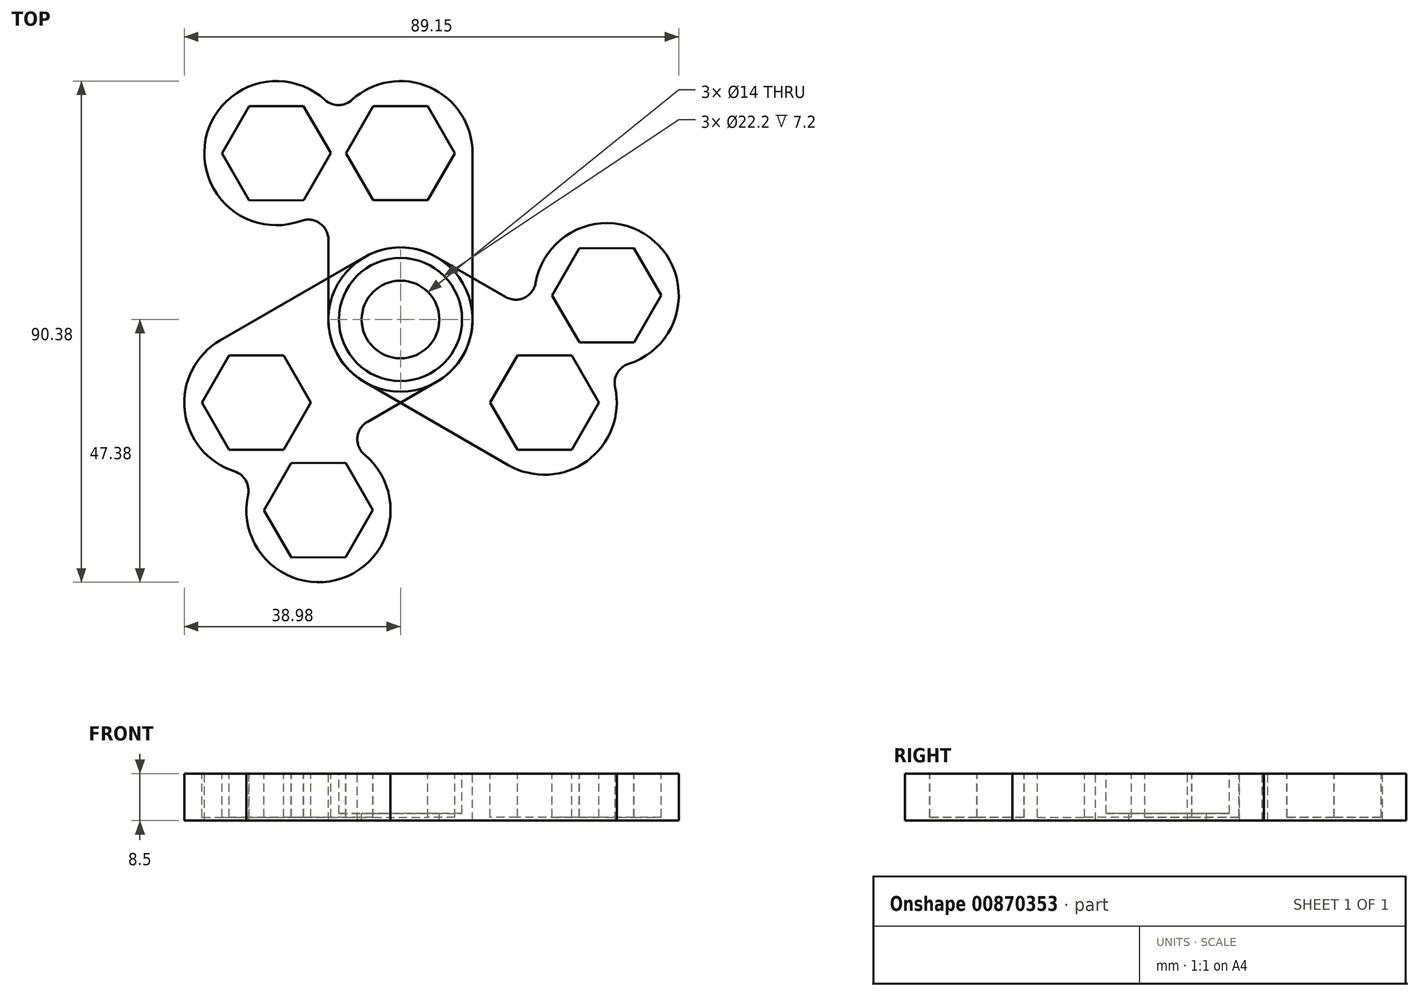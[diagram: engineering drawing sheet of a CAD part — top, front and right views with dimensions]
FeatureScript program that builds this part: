
annotation { "Feature Type Name" : "Feature", "Feature Type Description" : "" }
export const myFeature = defineFeature(function(context is Context, id is Id, definition is map)
    precondition{}
    {
        {
            var Q0;
            Q0=qCreatedBy(makeId("Top.planeOp"),FACE);
            var sketch = newSketch(context, id + "F0", { "sketchPlane" : qUnion([Q0])});
            skCircle(sketch, "E0", {"center": v(0, 0) * mm, "radius": 13 * mm});
            skCircle(sketch, "E1", {"center": v(0, 0) * mm, "radius": 11.1 * mm});
            skCircle(sketch, "E2.cCircle", {"center": v(0, 30) * mm, "radius": 8.5 * mm, "construction": true});
            skLineSegment(sketch, "E2.0", {"start": v(9.81, 30) * mm, "end": v(4.9, 21.5) * mm});
            skLineSegment(sketch, "E2.1", {"start": v(4.9, 21.5) * mm, "end": v(-4.9, 21.5) * mm});
            skLineSegment(sketch, "E2.2", {"start": v(-4.9, 21.5) * mm, "end": v(-9.81, 30) * mm});
            skLineSegment(sketch, "E2.3", {"start": v(-9.81, 30) * mm, "end": v(-4.9, 38.5) * mm});
            skLineSegment(sketch, "E2.4", {"start": v(-4.9, 38.5) * mm, "end": v(4.9, 38.5) * mm});
            skLineSegment(sketch, "E2.5", {"start": v(4.9, 38.5) * mm, "end": v(9.81, 30) * mm});
            skPoint(sketch, "E2.0.midPoint", {"position": v(7.36, 25.75) * mm});
            skCircle(sketch, "E3", {"center": v(0, 0) * mm, "radius": 7 * mm});
            skLineSegment(sketch, "E4", {"start": v(-13, 0) * mm, "end": v(-13, 21) * mm});
            skLineSegment(sketch, "E5", {"start": v(13, 0) * mm, "end": v(13, 30) * mm});
            skArc(sketch, "E6", {"start": v(-11.19, 36.62) * mm, "mid": v(-35.38, 30) * mm, "end": v(-11.19, 23.38) * mm});
            skLineSegment(sketch, "E7", {"start": v(-52.88, 30) * mm, "end": v(38.11, 30) * mm, "construction": true});
            skCircle(sketch, "E8.cCircle", {"center": v(-22.38, 30) * mm, "radius": 8.5 * mm, "construction": true});
            skLineSegment(sketch, "E8.0", {"start": v(-12.56, 30.03) * mm, "end": v(-17.44, 21.52) * mm});
            skLineSegment(sketch, "E8.1", {"start": v(-17.44, 21.52) * mm, "end": v(-27.26, 21.48) * mm});
            skLineSegment(sketch, "E8.2", {"start": v(-27.26, 21.48) * mm, "end": v(-32.2, 29.97) * mm});
            skLineSegment(sketch, "E8.3", {"start": v(-32.2, 29.97) * mm, "end": v(-27.31, 38.48) * mm});
            skLineSegment(sketch, "E8.4", {"start": v(-27.31, 38.48) * mm, "end": v(-17.5, 38.52) * mm});
            skLineSegment(sketch, "E8.5", {"start": v(-17.5, 38.52) * mm, "end": v(-12.56, 30.03) * mm});
            skPoint(sketch, "E8.0.midPoint", {"position": v(-15, 25.77) * mm});
            skArc(sketch, "E9.trimOffspring", {"start": v(-11.19, 23.38) * mm, "mid": v(13, 30) * mm, "end": v(-11.19, 36.62) * mm});
            skSolve(sketch);
        }
        {
            var Q0;
            {var subQ0=sQuery(id+"F0.wireOp",EDGE,"E4");Q0=makeQuery(id+"F0.imprint","IMPRINT",FACE,{"disambiguationData":[TD([[makeQuery(id+"F0.imprint","IMPRINT",EDGE,{"derivedFrom":subQ0}),-1.0]])]});}
            var Q1;
            Q1=makeQuery(id+"F0.imprint","IMPRINT",FACE,{"disambiguationData":[TD([[makeQuery(id+"F0.imprint","IMPRINT",EDGE,{"derivedFrom":sQuery(id+"F0.wireOp",EDGE,"E1")}),-1.0]])]});
            var Q2;
            Q2=makeQuery(id+"F0.imprint","IMPRINT",FACE,{"disambiguationData":[TD([[makeQuery(id+"F0.imprint","IMPRINT",EDGE,{"derivedFrom":sQuery(id+"F0.wireOp",EDGE,"E1")}),1.0]])]});
            var Q3;
            {var subQ3=sQuery(id+"F0.wireOp",EDGE,"E6");var subQ8=sQuery(id+"F0.wireOp",EDGE,"V23LrKdg-jynA-Owui-0Aw0-ESeFztE2tVGG");var subQ13=makeQuery(id+"F0.imprint","INTERSECT",VERTEX,{"disambiguationData":[OD(0.0)],"derivedFrom":[subQ8,subQ3]});Q3=makeQuery(id+"F0.imprint","IMPRINT",FACE,{"disambiguationData":[TD([[makeQuery(id+"F0.imprint","IMPRINT",EDGE,{"disambiguationData":[TD([[subQ13,-1.0]])],"derivedFrom":subQ8}),1.0]])]});}
            var Q4;
            {var subQ8=sQuery(id+"F0.wireOp",EDGE,"E8.1");Q4=makeQuery(id+"F0.imprint","IMPRINT",FACE,{"disambiguationData":[TD([[makeQuery(id+"F0.imprint","IMPRINT",EDGE,{"derivedFrom":subQ8}),1.0]])]});}
            var Q5;
            {var subQ0=sQuery(id+"F0.wireOp",EDGE,"E2.3");var subQ1=sQuery(id+"F0.wireOp",EDGE,"E2.2");var subQ2=makeQuery(id+"F0.imprint","INTERSECT",VERTEX,{"derivedFrom":[subQ1,subQ0]});Q5=makeQuery(id+"F0.imprint","IMPRINT",FACE,{"disambiguationData":[TD([[makeQuery(id+"F0.imprint","IMPRINT",EDGE,{"disambiguationData":[TD([[subQ2,1.0]])],"derivedFrom":subQ1}),-1.0]])]});}
            var Q6;
            Q6=makeQuery(id+"F0.imprint","IMPRINT",FACE,{"disambiguationData":[TD([[makeQuery(id+"F0.imprint","IMPRINT",EDGE,{"derivedFrom":sQuery(id+"F0.wireOp",EDGE,"E2.0")}),-1.0]])]});
            var Q7;
            {var subQ0=sQuery(id+"F0.wireOp",EDGE,"E8.1");Q7=makeQuery(id+"F0.imprint","IMPRINT",FACE,{"disambiguationData":[TD([[makeQuery(id+"F0.imprint","IMPRINT",EDGE,{"derivedFrom":subQ0}),-1.0]])]});}
            var Q8;
            {var subQ0=sQuery(id+"F0.wireOp",EDGE,"E8.0");var subQ1=sQuery(id+"F0.wireOp",EDGE,"V23LrKdg-jynA-Owui-0Aw0-ESeFztE2tVGG");var subQ2=makeQuery(id+"F0.imprint","INTERSECT",VERTEX,{"derivedFrom":[subQ1,subQ0]});Q8=makeQuery(id+"F0.imprint","IMPRINT",FACE,{"disambiguationData":[TD([[makeQuery(id+"F0.imprint","IMPRINT",EDGE,{"disambiguationData":[TD([[subQ2,-1.0]])],"derivedFrom":subQ1}),-1.0]])]});}
            var Q9;
            {var subQ0=sQuery(id+"F0.wireOp",EDGE,"V23LrKdg-jynA-Owui-0Aw0-ESeFztE2tVGG");var subQ1=makeQuery(id+"F0.imprint","INTERSECT",VERTEX,{"derivedFrom":[subQ0,sQuery(id+"F0.wireOp",EDGE,"E4")]});Q9=makeQuery(id+"F0.imprint","IMPRINT",FACE,{"disambiguationData":[TD([[makeQuery(id+"F0.imprint","IMPRINT",EDGE,{"disambiguationData":[TD([[subQ1,1.0]])],"derivedFrom":subQ0}),1.0]])]});}
            var Q10;
            Q10=makeQuery(id+"F0.imprint","IMPRINT",FACE,{"disambiguationData":[TD([[makeQuery(id+"F0.imprint","IMPRINT",EDGE,{"derivedFrom":sQuery(id+"F0.wireOp",EDGE,"E2.0")}),1.0]])]});
            var Q11;
            {var subQ0=sQuery(id+"F0.wireOp",EDGE,"E5");Q11=makeQuery(id+"F0.imprint","IMPRINT",FACE,{"disambiguationData":[TD([[makeQuery(id+"F0.imprint","IMPRINT",EDGE,{"derivedFrom":subQ0}),1.0]])]});}
            extrude(context, id + "F1", {"entities" : qUnion([Q0, Q1, Q2, Q3, Q4, Q5, Q6, Q7, Q8, Q9, Q10, Q11]), "oppositeDirection" : true, "depth" : 8.5 * mm, "offsetDistance" : 25 * mm});
        }
        {
            var Q0;
            Q0=makeQuery(id+"F0.imprint","IMPRINT",FACE,{"disambiguationData":[TD([[makeQuery(id+"F0.imprint","IMPRINT",EDGE,{"derivedFrom":sQuery(id+"F0.wireOp",EDGE,"E2.0")}),-1.0]])]});
            var Q1;
            {var subQ0=sQuery(id+"F0.wireOp",EDGE,"E2.3");var subQ1=sQuery(id+"F0.wireOp",EDGE,"E2.2");var subQ2=makeQuery(id+"F0.imprint","INTERSECT",VERTEX,{"derivedFrom":[subQ1,subQ0]});Q1=makeQuery(id+"F0.imprint","IMPRINT",FACE,{"disambiguationData":[TD([[makeQuery(id+"F0.imprint","IMPRINT",EDGE,{"disambiguationData":[TD([[subQ2,1.0]])],"derivedFrom":subQ1}),-1.0]])]});}
            var Q2;
            {var subQ0=sQuery(id+"F0.wireOp",EDGE,"E8.1");Q2=makeQuery(id+"F0.imprint","IMPRINT",FACE,{"disambiguationData":[TD([[makeQuery(id+"F0.imprint","IMPRINT",EDGE,{"derivedFrom":subQ0}),-1.0]])]});}
            var Q3;
            {var subQ0=sQuery(id+"F0.wireOp",EDGE,"V23LrKdg-jynA-Owui-0Aw0-ESeFztE2tVGG");var subQ1=makeQuery(id+"F0.imprint","INTERSECT",VERTEX,{"derivedFrom":[subQ0,sQuery(id+"F0.wireOp",EDGE,"E4")]});Q3=makeQuery(id+"F0.imprint","IMPRINT",FACE,{"disambiguationData":[TD([[makeQuery(id+"F0.imprint","IMPRINT",EDGE,{"disambiguationData":[TD([[subQ1,1.0]])],"derivedFrom":subQ0}),1.0]])]});}
            extrude(context, id + "F2", {"entities" : qUnion([Q0, Q1, Q2, Q3]), "operationType" : NewBodyOperationType.REMOVE, "oppositeDirection" : true, "depth" : 7.9 * mm, "offsetDistance" : 25 * mm});
        }
        {
            var Q0;
            Q0=makeQuery(id+"F0.imprint","IMPRINT",FACE,{"disambiguationData":[TD([[makeQuery(id+"F0.imprint","IMPRINT",EDGE,{"derivedFrom":sQuery(id+"F0.wireOp",EDGE,"E1")}),1.0]])]});
            extrude(context, id + "F3", {"entities" : qUnion([Q0]), "operationType" : NewBodyOperationType.REMOVE, "oppositeDirection" : true, "depth" : 7.2 * mm, "offsetDistance" : 25 * mm});
        }
        {
            var Q0;
            Q0=makeQuery(id+"F1.opExtrude","SWEPT_BODY",BODY,{"disambiguationData":[OSD([sQuery(id+"F0.wireOp",EDGE,"E0"),sQuery(id+"F0.wireOp",EDGE,"V23LrKdg-jynA-Owui-0Aw0-ESeFztE2tVGG"),sQuery(id+"F0.wireOp",EDGE,"E3"),sQuery(id+"F0.wireOp",EDGE,"E4"),sQuery(id+"F0.wireOp",EDGE,"E5")])]});
            var Q1;
            Q1=makeQuery(id+"F3.boolean.opBoolean","COPY",FACE,{"derivedFrom":makeQuery(id+"F3.opExtrude","SWEPT_FACE",FACE,{"disambiguationData":[OSD([sQuery(id+"F0.wireOp",EDGE,"E1")])]})});
            circularPattern(context, id + "F4", {"entities" : qUnion([Q0]), "axis" : qUnion([Q1]), "angle" : 360 * degree, "instanceCount" : 3, "equalSpace" : true});
        }
        {
            var Q0;
            Q0=makeQuery(id+"F1.opExtrude","SWEPT_EDGE",EDGE,{"disambiguationData":[OSD([sQuery(id+"F0.wireOp",EDGE,"E4"),sQuery(id+"F0.wireOp",EDGE,"E6")])]});
            var Q1;
            Q1=makeQuery(id+"F1.opExtrude","SWEPT_EDGE",EDGE,{"disambiguationData":[OSD([sQuery(id+"F0.wireOp",EDGE,"E6"),sQuery(id+"F0.wireOp",EDGE,"E9.trimOffspring")])]});
            var Q2;
            Q2=makeQuery(id+"F4.opPattern","COPY",EDGE,{"derivedFrom":makeQuery(id+"F1.opExtrude","SWEPT_EDGE",EDGE,{"disambiguationData":[OSD([sQuery(id+"F0.wireOp",EDGE,"E4"),sQuery(id+"F0.wireOp",EDGE,"E6")])]}),"instanceName":"1"});
            var Q3;
            Q3=makeQuery(id+"F4.opPattern","COPY",EDGE,{"derivedFrom":makeQuery(id+"F1.opExtrude","SWEPT_EDGE",EDGE,{"disambiguationData":[OSD([sQuery(id+"F0.wireOp",EDGE,"E6"),sQuery(id+"F0.wireOp",EDGE,"E9.trimOffspring")])]}),"instanceName":"1"});
            var Q4;
            Q4=makeQuery(id+"F4.opPattern","COPY",EDGE,{"derivedFrom":makeQuery(id+"F1.opExtrude","SWEPT_EDGE",EDGE,{"disambiguationData":[OSD([sQuery(id+"F0.wireOp",EDGE,"E6"),sQuery(id+"F0.wireOp",EDGE,"E9.trimOffspring")])]}),"instanceName":"2"});
            var Q5;
            Q5=makeQuery(id+"F4.opPattern","COPY",EDGE,{"derivedFrom":makeQuery(id+"F1.opExtrude","SWEPT_EDGE",EDGE,{"disambiguationData":[OSD([sQuery(id+"F0.wireOp",EDGE,"E4"),sQuery(id+"F0.wireOp",EDGE,"E6")])]}),"instanceName":"2"});
            fillet(context, id + "F5", {"entities" : qUnion([Q0, Q1, Q2, Q3, Q4, Q5]), "radius" : 3.63 * mm, "tangentPropagation" : true, "allowEdgeOverflow" : false});
        }
    });
